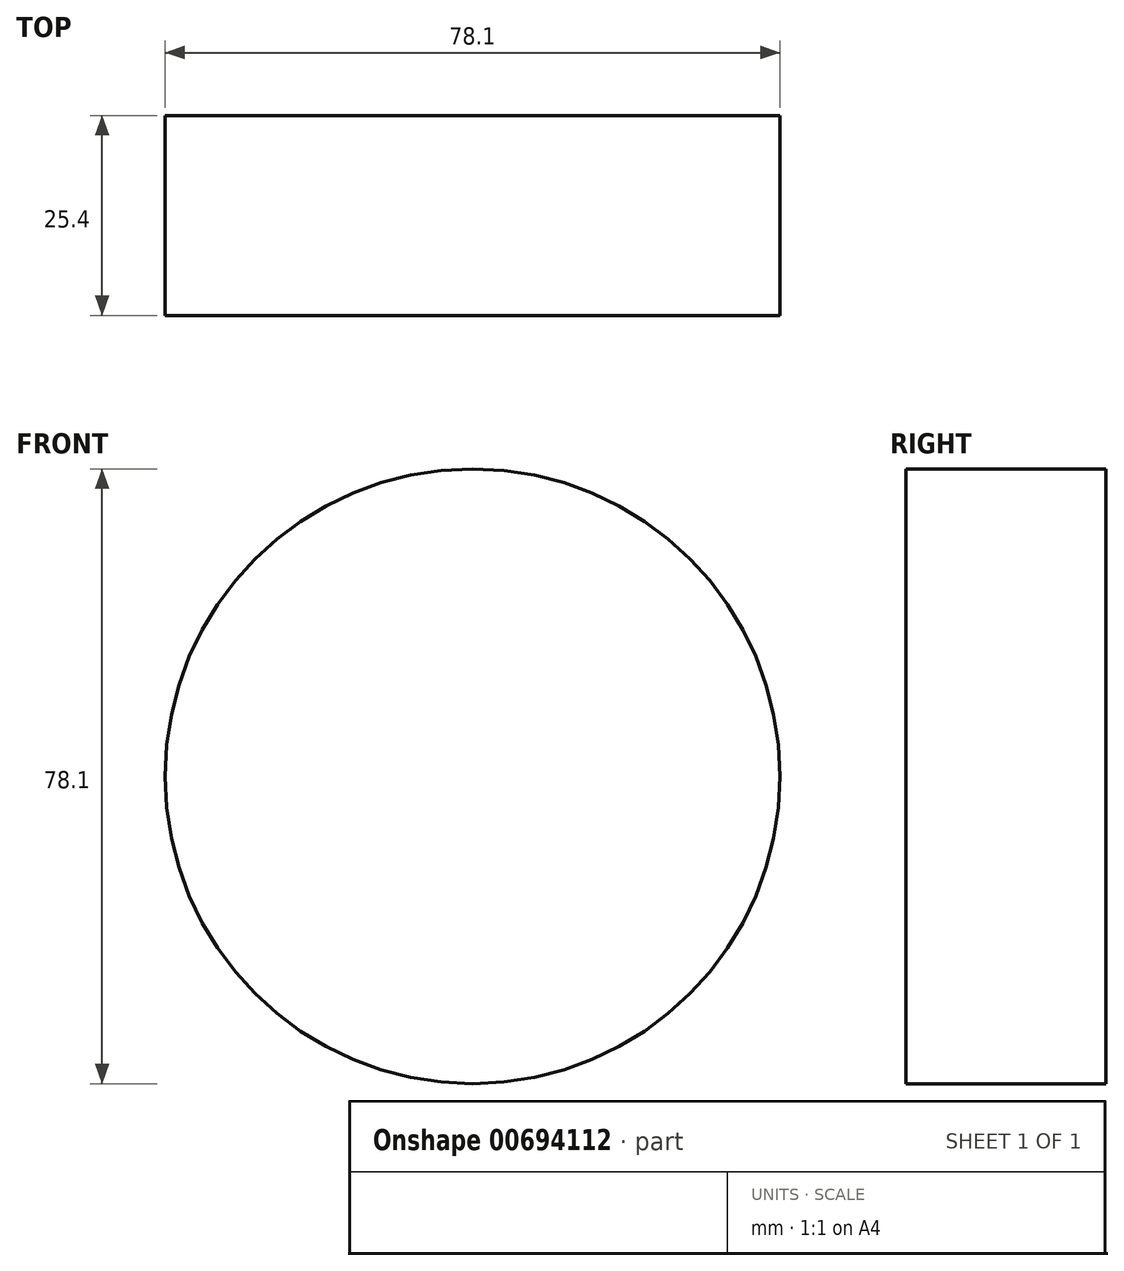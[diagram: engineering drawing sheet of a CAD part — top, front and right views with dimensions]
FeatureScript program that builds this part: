
annotation { "Feature Type Name" : "Feature", "Feature Type Description" : "" }
export const myFeature = defineFeature(function(context is Context, id is Id, definition is map)
    precondition{}
    {
        {
            var Q0;
            Q0=qCreatedBy(makeId("Front.planeOp"),FACE);
            var sketch = newSketch(context, id + "F0", { "sketchPlane" : qUnion([Q0])});
            skCircle(sketch, "E0", {"center": v(0, 0) * mm, "radius": 39.05 * mm});
            skSolve(sketch);
        }
        {
            var Q0;
            Q0=makeQuery(id+"F0.imprint","IMPRINT",FACE,{"disambiguationData":[TD([[makeQuery(id+"F0.imprint","IMPRINT",EDGE,{"derivedFrom":sQuery(id+"F0.wireOp",EDGE,"E0")}),1.0]])]});
            extrude(context, id + "F1", {"entities" : qUnion([Q0]), "depth" : 25.4 * mm, "offsetDistance" : 25.4 * mm});
        }
    });
